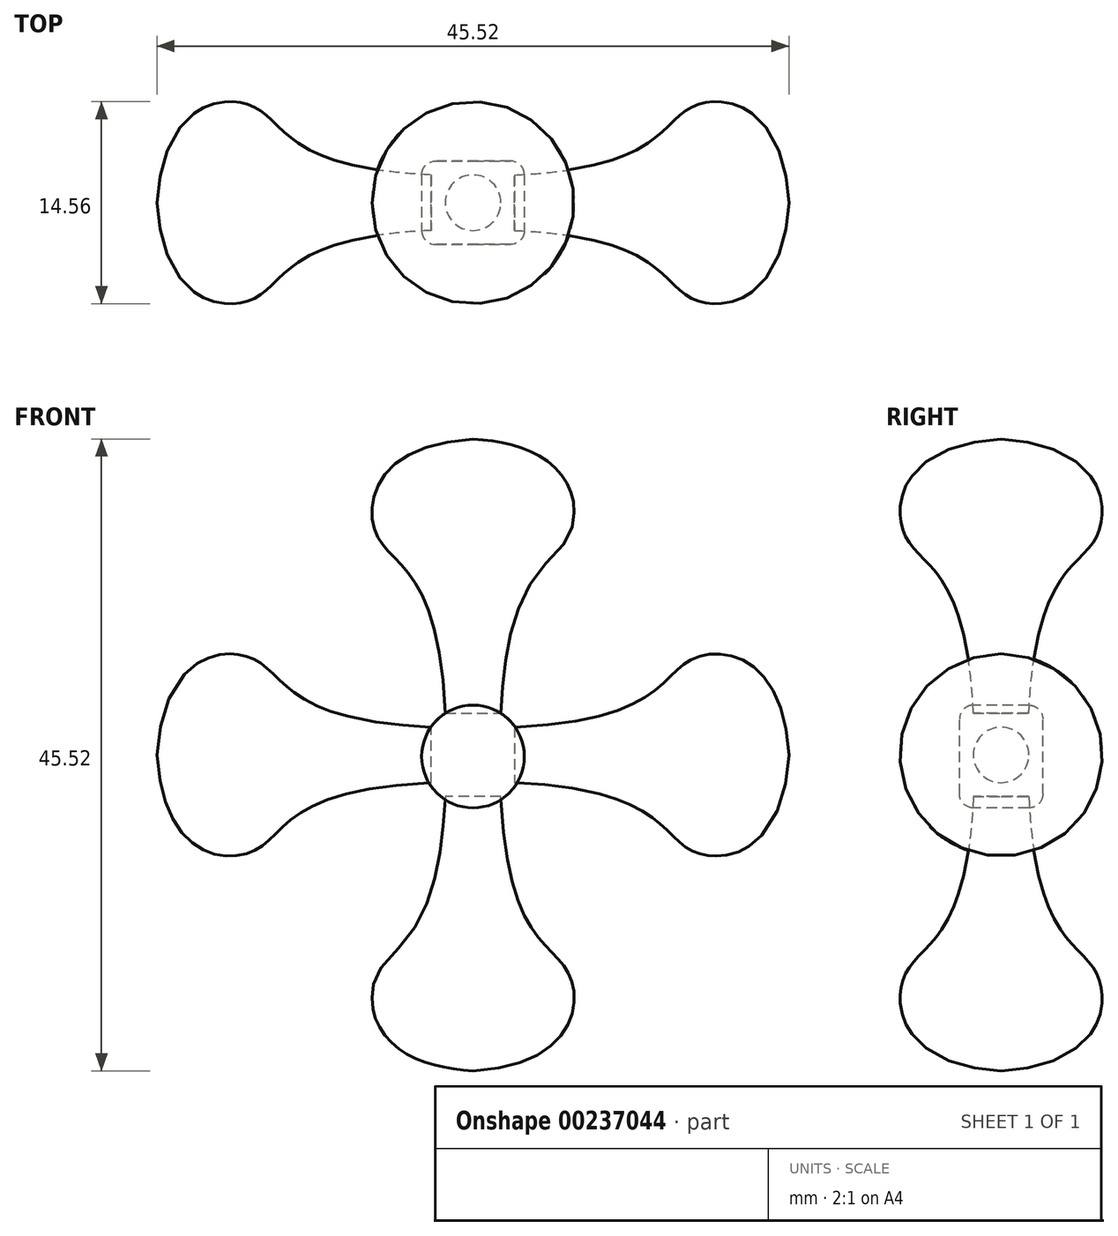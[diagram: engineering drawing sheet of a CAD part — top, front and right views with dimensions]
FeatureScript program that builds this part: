
annotation { "Feature Type Name" : "Feature", "Feature Type Description" : "" }
export const myFeature = defineFeature(function(context is Context, id is Id, definition is map)
    precondition{}
    {
        {
            var Q0;
            Q0=qCreatedBy(makeId("Front.planeOp"),FACE);
            var sketch = newSketch(context, id + "F0", { "sketchPlane" : qUnion([Q0])});
            skLineSegment(sketch, "E0", {"start": v(0, 22.76) * mm, "end": v(0, 21.76) * mm, "construction": true});
            skLineSegment(sketch, "E1", {"start": v(-17.5, 0) * mm, "end": v(17.5, 0) * mm, "construction": true});
            skCircle(sketch, "E2", {"center": v(0, 0) * mm, "radius": 53.53 * mm, "construction": true});
            skFitSpline(sketch, "E3", {"points": [v(0, 22.76) * mm, v(-7, 16) * mm, v(-2, 3) * mm], "startDerivative": vector(-46.48, -2.52) * mm, "endDerivative": vector(2.67, -59.56) * mm});
            skLineSegment(sketch, "E4", {"start": v(-2, 3) * mm, "end": v(0, 3) * mm});
            skLineSegment(sketch, "E5", {"start": v(0, 3) * mm, "end": v(0, 22.76) * mm});
            skLineSegment(sketch, "E6", {"start": v(0, 4) * mm, "end": v(-1, 4) * mm});
            skFitSpline(sketch, "E7", {"points": [v(-1, 4) * mm, v(-5.7, 16) * mm, v(0, 21.76) * mm], "startDerivative": vector(-9.8, 62.39) * mm, "endDerivative": vector(47.85, 5.53) * mm});
            skLineSegment(sketch, "E8.trimOffspring", {"start": v(0, 4) * mm, "end": v(0, -22.5) * mm, "construction": true});
            skSolve(sketch);
        }
        {
            var Q0;
            Q0 = qSketchRegion(id + "F0", true);
            var Q1;
            Q1=sQuery(id+"F0.wireOp",EDGE,"E5");
            revolve(context, id + "F1", {"entities" : qUnion([Q0]), "axis" : qUnion([Q1]), "revolveType" : RevolveType.FULL});
        }
        {
            var Q0;
            Q0=makeQuery(id+"F1.opRevolve","SWEPT_BODY",BODY,{"disambiguationData":[OSD([sQuery(id+"F0.wireOp",EDGE,"E3"),sQuery(id+"F0.wireOp",EDGE,"E4"),sQuery(id+"F0.wireOp",EDGE,"E5")])]});
            var Q1;
            Q1=sQuery(id+"F0.wireOp",EDGE,"E2");
            circularPattern(context, id + "F2", {"entities" : qUnion([Q0]), "axis" : qUnion([Q1]), "angle" : 360 * degree, "instanceCount" : 4, "equalSpace" : true});
        }
        {
            var Q0;
            Q0=qCreatedBy(makeId("Front.planeOp"),FACE);
            var sketch = newSketch(context, id + "F3", { "sketchPlane" : qUnion([Q0])});
            skLineSegment(sketch, "E9.0", {"start": v(2, 3) * mm, "end": v(-2, 3) * mm});
            skLineSegment(sketch, "E10.0", {"start": v(3, -2) * mm, "end": v(3, 2) * mm});
            skLineSegment(sketch, "E11.0", {"start": v(-2, -3) * mm, "end": v(2, -3) * mm});
            skLineSegment(sketch, "E12.0", {"start": v(-3, 2) * mm, "end": v(-3, -2) * mm});
            skCircle(sketch, "E13", {"center": v(0, -0.11) * mm, "radius": 3.7 * mm});
            skSolve(sketch);
        }
        {
            var Q0;
            Q0 = qSketchRegion(id + "F3", true);
            extrude(context, id + "F4", {"entities" : qUnion([Q0]), "endBound" : BoundingType.SYMMETRIC, "oppositeDirection" : true, "depth" : 6 * mm});
        }
        {
            var Q0;
            Q0=makeQuery(id+"F4.opExtrude","CAP_FACE",FACE,{"disambiguationData":[OSD([sQuery(id+"F3.wireOp",EDGE,"E13")])],"isStart":true});
            var Q1;
            Q1=makeQuery(id+"F4.opExtrude","CAP_EDGE",EDGE,{"disambiguationData":[OSD([sQuery(id+"F3.wireOp",EDGE,"E13")])],"isStart":true});
            var Q2;
            Q2=makeQuery(id+"F4.opExtrude","CAP_EDGE",EDGE,{"disambiguationData":[OSD([sQuery(id+"F3.wireOp",EDGE,"E13")])],"isStart":false});
            fillet(context, id + "F5", {"entities" : qUnion([Q0, Q1, Q2]), "radius" : 1 * mm, "tangentPropagation" : true, "allowEdgeOverflow" : false});
        }
    });
